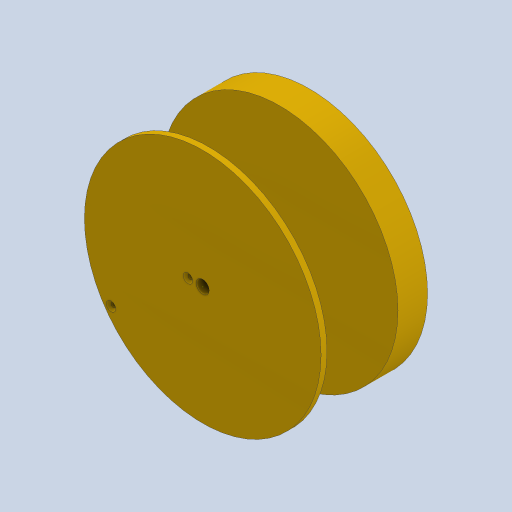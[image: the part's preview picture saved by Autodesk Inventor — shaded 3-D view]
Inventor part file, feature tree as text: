
AUTODESK INVENTOR PART (.ipt)
format: ipt  version: 2024 (Build 280153000, 153)  size: 296,448 bytes
history: native  units: in
note: dims shown in document units (in); Inventor stores cm internally (conversion verified against a paired STEP export)
features: extrude x5, sketch x2, hole x2, other x2, chamfer x1, loft x1
ambient origin geometry x8: Origin, YZ Plane, XZ Plane, XY Plane, X Axis, Y Axis, Z Axis, Center Point
bodies: Solid1 (feature_tree), Solid2 (feature_tree)
feature tree (13):
  extrude  "Extrusion1"  Depth=0.1969in TaperAngle=0.0deg
  extrude  "Extrusion2"  Depth=0.4724in TaperAngle=0.0deg
  extrude  "Extrusion3"  Depth=0.189in
  extrude  "Extrusion4"  Depth=0.0394in TaperAngle=0.0deg
  sketch  "Sketch6"  dims[d0=1.5748in d1=0.1969in d2=0.0in]
  extrude  "Extrusion5"  Depth=0.189in
  chamfer  "Chamfer1"  Distance=0.2028in
  hole  "Hole3"  [1 undecoded]
  hole  "Hole4"  [1 undecoded]
  loft  "Loft1"
  sketch  "Sketch12"  dims[d3=0.1575in d4=0.4724in d5=0.0in d6=1.5748in d7=0.0394in d8=0.0in d9=0.0866in d10=0.2028in d11=0.0in d20=0.0315in d21=0.0315in d22=0.0591in d23=0.0in d24=0.0157in d25=0.0787in d26=45.0deg d38=0.0984in d39=0.6102in d40=1.0433in d41=0.1969in d42=0.1969in d43=1.0433in d44=0.0617in d45=0.1575in d46=0.1575in d47=0.0787in d48=90.0deg d49=0.248in d50=0.8108in d55=0.1969in d56=0.1969in d57=0.0968in d58=0.2362in d59=0.1575in d60=0.0787in d61=90.0deg d62=0.189in d63=0.0in d64=0.0in d65=90.0deg d66=0.0in d67=90.0deg]
  other  "Edges1"
  other  "Edges2"
note: 2 required parameter values undecoded (feature->parameter linkage not recoverable at this tier; creation-order binding heuristic only, values carry confidence <= 0.55)
